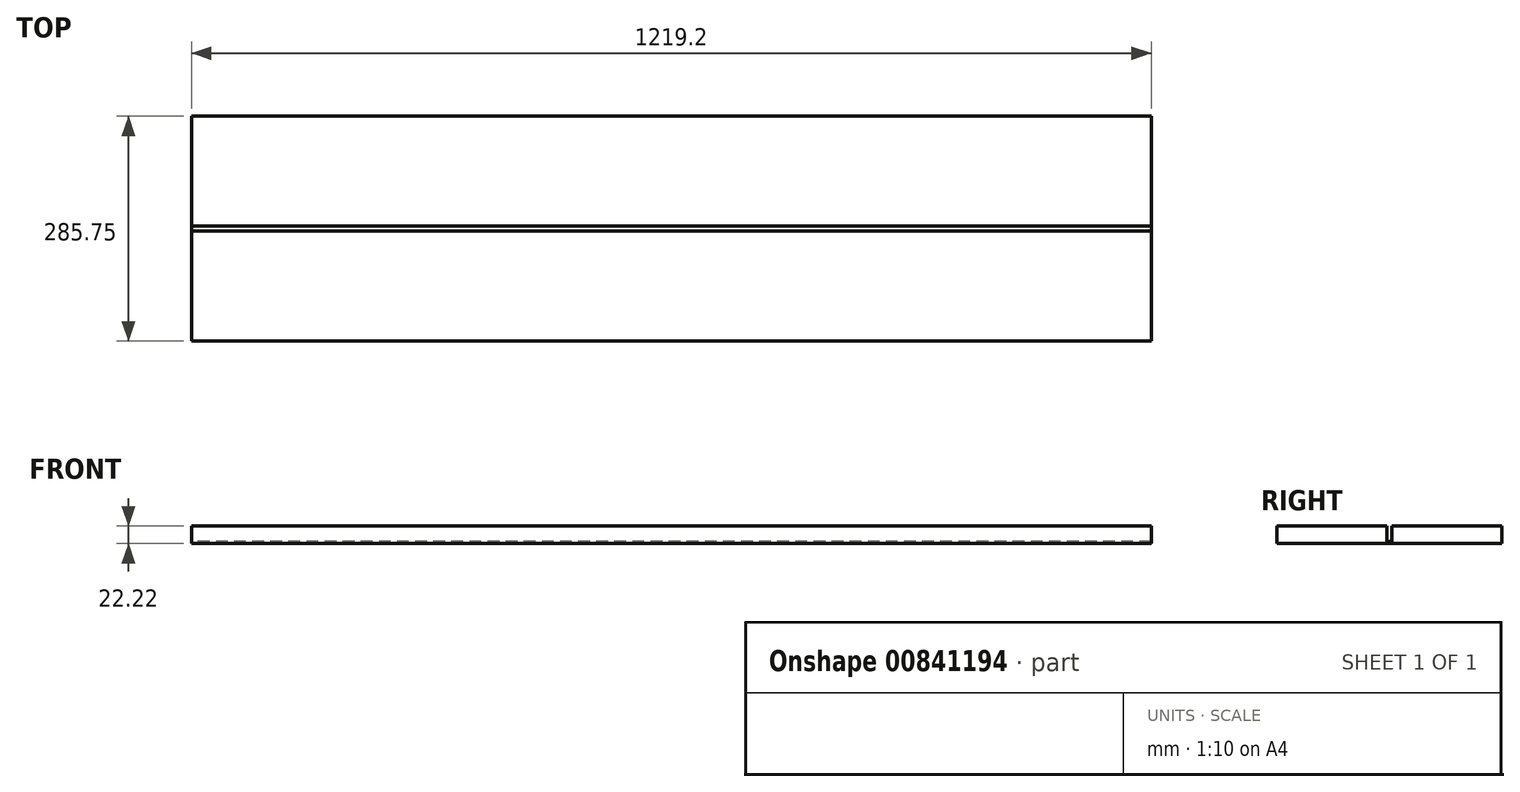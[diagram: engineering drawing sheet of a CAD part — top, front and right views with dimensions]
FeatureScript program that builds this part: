
annotation { "Feature Type Name" : "Feature", "Feature Type Description" : "" }
export const myFeature = defineFeature(function(context is Context, id is Id, definition is map)
    precondition{}
    {
        {
            var Q0;
            Q0=qCreatedBy(makeId("Right.planeOp"),FACE);
            var sketch = newSketch(context, id + "F0", { "sketchPlane" : qUnion([Q0])});
            skLineSegment(sketch, "E0.bottom", {"start": v(69.85, -11.11) * mm, "end": v(-69.85, -11.11) * mm});
            skLineSegment(sketch, "E0.top", {"start": v(69.85, 11.11) * mm, "end": v(-69.85, 11.11) * mm});
            skLineSegment(sketch, "E0.left", {"start": v(69.85, -8.57) * mm, "end": v(69.85, 11.11) * mm});
            skLineSegment(sketch, "E0.right", {"start": v(-69.85, -11.11) * mm, "end": v(-69.85, 11.11) * mm});
            skPoint(sketch, "E0.middle", {"position": v(0, 0) * mm});
            skLineSegment(sketch, "E1.bottom", {"start": v(76.2, 11.11) * mm, "end": v(215.9, 11.11) * mm});
            skLineSegment(sketch, "E1.top", {"start": v(76.2, -11.11) * mm, "end": v(215.9, -11.11) * mm});
            skLineSegment(sketch, "E1.left", {"start": v(76.2, 11.11) * mm, "end": v(76.2, -8.57) * mm});
            skLineSegment(sketch, "E1.right", {"start": v(215.9, 11.11) * mm, "end": v(215.9, -11.11) * mm});
            skLineSegment(sketch, "E2", {"start": v(69.85, -8.57) * mm, "end": v(76.2, -8.57) * mm});
            skLineSegment(sketch, "E3", {"start": v(69.85, -11.11) * mm, "end": v(76.2, -11.11) * mm});
            skSolve(sketch);
        }
        {
            var Q0;
            Q0=makeQuery(id+"F0.imprint","IMPRINT",FACE,{"disambiguationData":[TD([[makeQuery(id+"F0.imprint","IMPRINT",EDGE,{"derivedFrom":sQuery(id+"F0.wireOp",EDGE,"E0.bottom")}),-1.0]])]});
            var Q1;
            Q1=makeQuery(id+"F0.imprint","IMPRINT",FACE,{"disambiguationData":[TD([[makeQuery(id+"F0.imprint","IMPRINT",EDGE,{"derivedFrom":sQuery(id+"F0.wireOp",EDGE,"E1.bottom")}),-1.0]])]});
            extrude(context, id + "F1", {"entities" : qUnion([Q0, Q1]), "depth" : 1219.2 * mm, "offsetDistance" : 25.4 * mm});
        }
    });
